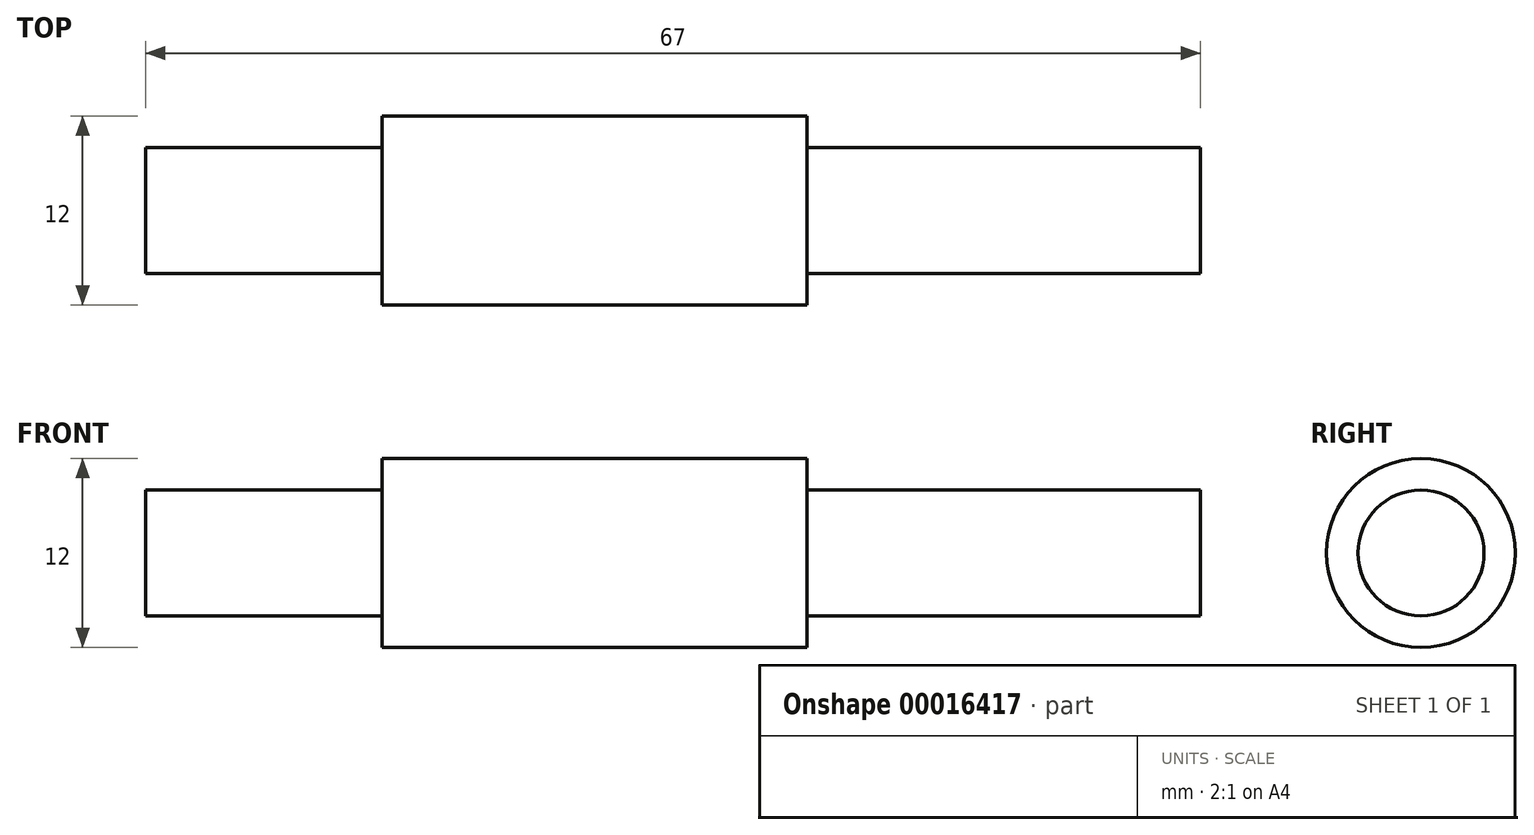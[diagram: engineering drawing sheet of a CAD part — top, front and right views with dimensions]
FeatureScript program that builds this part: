
annotation { "Feature Type Name" : "Feature", "Feature Type Description" : "" }
export const myFeature = defineFeature(function(context is Context, id is Id, definition is map)
    precondition{}
    {
        {
            var Q0;
            Q0=qCreatedBy(makeId("Front.planeOp"),FACE);
            var sketch = newSketch(context, id + "F0", { "sketchPlane" : qUnion([Q0])});
            skLineSegment(sketch, "E0.0", {"start": v(19.57, -3.7) * mm, "end": v(-47.43, -3.7) * mm});
            skLineSegment(sketch, "E1.bottom", {"start": v(-32.43, 2.3) * mm, "end": v(-5.43, 2.3) * mm});
            skLineSegment(sketch, "E2", {"start": v(-5.43, 2.3) * mm, "end": v(-5.43, 0.3) * mm});
            skLineSegment(sketch, "E3.0", {"start": v(19.57, 0.3) * mm, "end": v(19.57, -3.7) * mm});
            skLineSegment(sketch, "E4.0", {"start": v(-47.43, 0.3) * mm, "end": v(-47.43, -3.7) * mm});
            skLineSegment(sketch, "E5.0", {"start": v(-32.43, 2.3) * mm, "end": v(-32.43, 0.3) * mm});
            skLineSegment(sketch, "E6.0", {"start": v(19.57, 0.3) * mm, "end": v(-5.43, 0.3) * mm});
            skLineSegment(sketch, "E7.trimOffspring", {"start": v(-32.43, 0.3) * mm, "end": v(-47.43, 0.3) * mm});
            skSolve(sketch);
        }
        {
            var Q0;
            Q0=makeQuery(id+"F0.imprint","IMPRINT",FACE,{"disambiguationData":[TD([[makeQuery(id+"F0.imprint","IMPRINT",EDGE,{"derivedFrom":sQuery(id+"F0.wireOp",EDGE,"E0.0")}),-1.0]])]});
            var Q1;
            Q1=sQuery(id+"F0.wireOp",EDGE,"E0.0");
            revolve(context, id + "F1", {"entities" : qUnion([Q0]), "axis" : qUnion([Q1]), "revolveType" : RevolveType.FULL});
        }
    });
